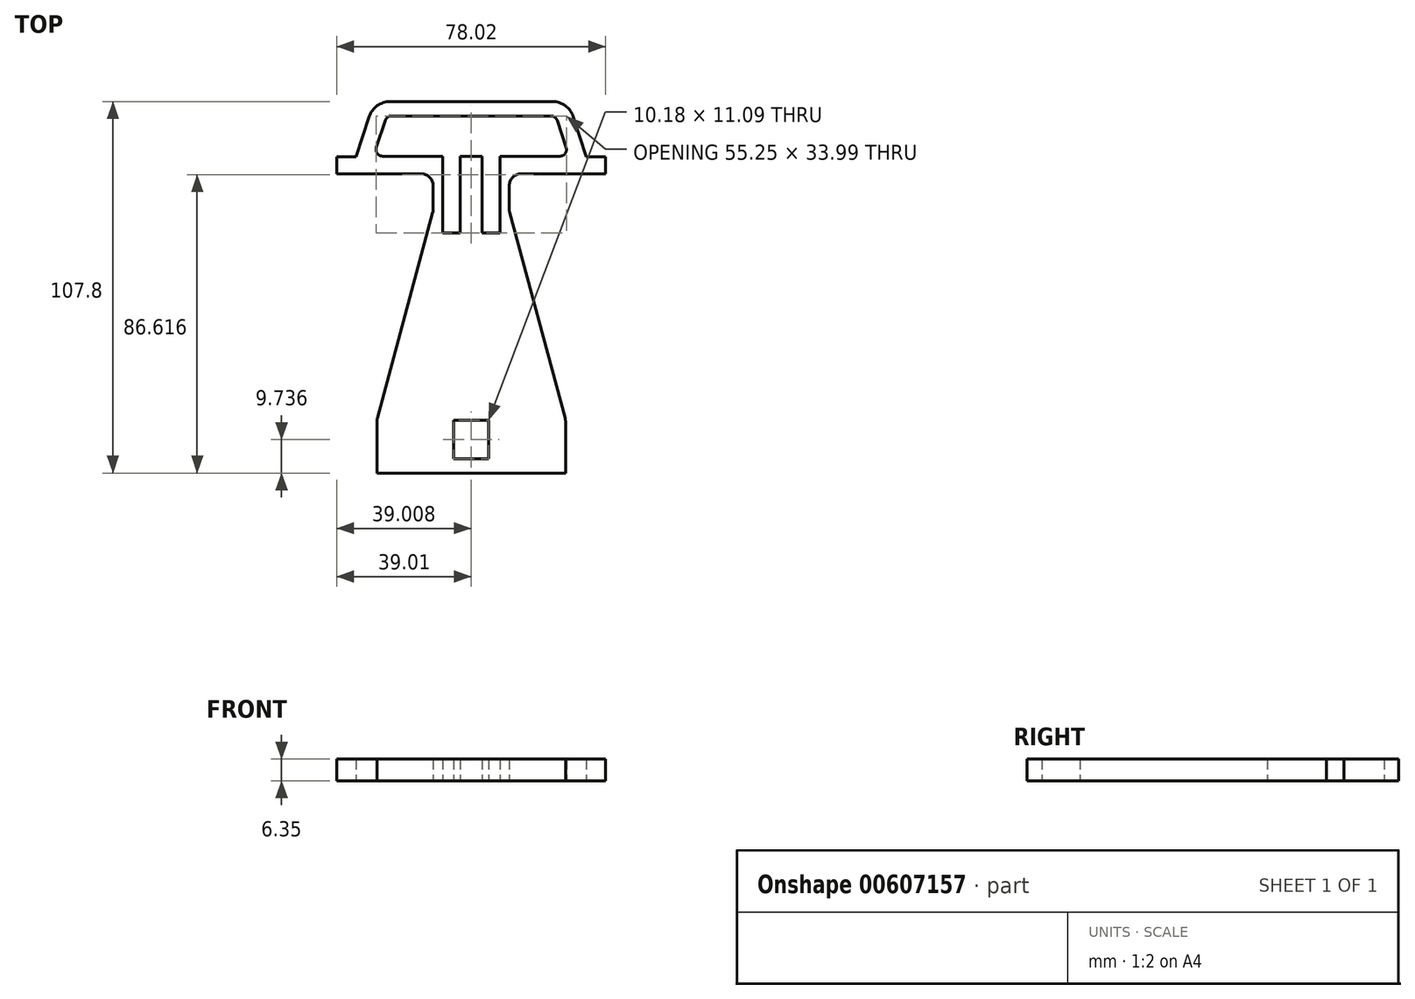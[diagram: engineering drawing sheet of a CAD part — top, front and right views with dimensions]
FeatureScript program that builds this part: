
annotation { "Feature Type Name" : "Feature", "Feature Type Description" : "" }
export const myFeature = defineFeature(function(context is Context, id is Id, definition is map)
    precondition{}
    {
        {
            var Q0;
            Q0=qCreatedBy(makeId("Top.planeOp"),FACE);
            var sketch = newSketch(context, id + "F0", { "sketchPlane" : qUnion([Q0])});
            skLineSegment(sketch, "E0", {"start": v(0, 65.32) * mm, "end": v(0, -59.25) * mm, "construction": true});
            skLineSegment(sketch, "E1", {"start": v(-31.53, 41.22) * mm, "end": v(-25.33, 41.22) * mm});
            skLineSegment(sketch, "E2.MirrorCS", {"start": v(31.53, 41.22) * mm, "end": v(25.33, 41.22) * mm});
            skLineSegment(sketch, "E3", {"start": v(-25.74, 46.3) * mm, "end": v(0, 46.3) * mm});
            skLineSegment(sketch, "E4.MirrorCS", {"start": v(25.72, 46.3) * mm, "end": v(0, 46.3) * mm});
            skPoint(sketch, "E5.visualSharp", {"position": v(-15.2, 41.22) * mm});
            skPoint(sketch, "E6.visualSharp", {"position": v(15.2, 41.22) * mm});
            skLineSegment(sketch, "E7", {"start": v(-33.42, 43.12) * mm, "end": v(-33.42, 46.18) * mm});
            skLineSegment(sketch, "E8", {"start": v(-33.42, 46.18) * mm, "end": v(-29.59, 57.8) * mm});
            skLineSegment(sketch, "E9", {"start": v(-23.56, 62.16) * mm, "end": v(0, 62.16) * mm});
            skLineSegment(sketch, "E10", {"start": v(-27.54, 48.79) * mm, "end": v(-24.93, 56.67) * mm});
            skLineSegment(sketch, "E11", {"start": v(-23.14, 57.97) * mm, "end": v(0, 57.97) * mm});
            skLineSegment(sketch, "E12.MirrorCS", {"start": v(33.42, 43.12) * mm, "end": v(33.42, 46.18) * mm});
            skLineSegment(sketch, "E13.MirrorCS", {"start": v(33.42, 46.18) * mm, "end": v(29.59, 57.8) * mm});
            skLineSegment(sketch, "E14.MirrorCS", {"start": v(23.56, 62.16) * mm, "end": v(0, 62.16) * mm});
            skLineSegment(sketch, "E15.MirrorCS", {"start": v(23.14, 57.97) * mm, "end": v(0, 57.97) * mm});
            skLineSegment(sketch, "E16.MirrorCS", {"start": v(27.53, 48.8) * mm, "end": v(24.93, 56.67) * mm});
            skPoint(sketch, "E17.visualSharp", {"position": v(-28.15, 62.16) * mm});
            skArc(sketch, "E17.filletArc", {"start": v(-23.56, 62.16) * mm, "mid": v(-27.28, 60.95) * mm, "end": v(-29.59, 57.8) * mm});
            skPoint(sketch, "E18.visualSharp", {"position": v(28.15, 62.16) * mm});
            skArc(sketch, "E18.filletArc", {"start": v(29.59, 57.8) * mm, "mid": v(27.28, 60.95) * mm, "end": v(23.56, 62.16) * mm});
            skPoint(sketch, "E19.visualSharp", {"position": v(-33.42, 41.22) * mm});
            skArc(sketch, "E19.filletArc", {"start": v(-33.42, 43.12) * mm, "mid": v(-32.87, 41.78) * mm, "end": v(-31.53, 41.22) * mm});
            skPoint(sketch, "E20.visualSharp", {"position": v(33.42, 41.22) * mm});
            skArc(sketch, "E20.filletArc", {"start": v(31.53, 41.22) * mm, "mid": v(32.87, 41.78) * mm, "end": v(33.42, 43.12) * mm});
            skPoint(sketch, "E21.visualSharp", {"position": v(-28.36, 46.3) * mm});
            skArc(sketch, "E21.filletArc", {"start": v(-27.54, 48.79) * mm, "mid": v(-27.27, 47.09) * mm, "end": v(-25.74, 46.3) * mm});
            skPoint(sketch, "E22.visualSharp", {"position": v(-24.5, 57.97) * mm});
            skArc(sketch, "E22.filletArc", {"start": v(-23.14, 57.97) * mm, "mid": v(-24.24, 57.6) * mm, "end": v(-24.93, 56.67) * mm});
            skPoint(sketch, "E23.visualSharp", {"position": v(24.5, 57.97) * mm});
            skArc(sketch, "E23.filletArc", {"start": v(24.93, 56.67) * mm, "mid": v(24.24, 57.6) * mm, "end": v(23.14, 57.97) * mm});
            skPoint(sketch, "E24.visualSharp", {"position": v(28.36, 46.3) * mm});
            skArc(sketch, "E24.filletArc", {"start": v(25.72, 46.3) * mm, "mid": v(27.27, 47.1) * mm, "end": v(27.53, 48.8) * mm});
            skLineSegment(sketch, "E25", {"start": v(-25.33, 41.22) * mm, "end": v(-14.55, 41.22) * mm});
            skLineSegment(sketch, "E26", {"start": v(-11.03, 37.7) * mm, "end": v(-11.03, 30.91) * mm});
            skLineSegment(sketch, "E27", {"start": v(-11.15, 30) * mm, "end": v(-27.22, -29.67) * mm});
            skLineSegment(sketch, "E28", {"start": v(-31.53, -45.64) * mm, "end": v(0, -45.64) * mm});
            skLineSegment(sketch, "E29.MirrorCS", {"start": v(11.03, 37.7) * mm, "end": v(11.03, 30.91) * mm});
            skLineSegment(sketch, "E30.MirrorCS", {"start": v(25.33, 41.22) * mm, "end": v(14.55, 41.22) * mm});
            skLineSegment(sketch, "E31.MirrorCS", {"start": v(11.15, 30) * mm, "end": v(27.22, -29.67) * mm});
            skLineSegment(sketch, "E32.MirrorCS", {"start": v(31.53, -45.64) * mm, "end": v(0, -45.64) * mm});
            skPoint(sketch, "E33.visualSharp", {"position": v(-11.03, 41.22) * mm});
            skArc(sketch, "E33.filletArc", {"start": v(-11.03, 37.7) * mm, "mid": v(-12.06, 40.19) * mm, "end": v(-14.55, 41.22) * mm});
            skPoint(sketch, "E34.visualSharp", {"position": v(11.03, 41.22) * mm});
            skArc(sketch, "E34.filletArc", {"start": v(14.55, 41.22) * mm, "mid": v(12.06, 40.19) * mm, "end": v(11.03, 37.7) * mm});
            skPoint(sketch, "E35.visualSharp", {"position": v(11.03, 30.45) * mm});
            skArc(sketch, "E35.filletArc", {"start": v(11.03, 30.91) * mm, "mid": v(11.06, 30.45) * mm, "end": v(11.15, 30) * mm});
            skPoint(sketch, "E36.visualSharp", {"position": v(-11.03, 30.45) * mm});
            skArc(sketch, "E36.filletArc", {"start": v(-11.15, 30) * mm, "mid": v(-11.06, 30.45) * mm, "end": v(-11.03, 30.91) * mm});
            skLineSegment(sketch, "E37", {"start": v(-27.35, -30.58) * mm, "end": v(-27.35, -68.57) * mm});
            skLineSegment(sketch, "E38.MirrorCS", {"start": v(27.35, -30.58) * mm, "end": v(27.35, -68.57) * mm});
            skPoint(sketch, "E39.newPointA", {"position": v(-31.53, -45.64) * mm});
            skPoint(sketch, "E39.newPointB", {"position": v(-27.35, 4.35) * mm});
            skArc(sketch, "E39.filletArc", {"start": v(-27.22, -29.67) * mm, "mid": v(-27.31, -30.12) * mm, "end": v(-27.35, -30.58) * mm});
            skPoint(sketch, "E40.newPointA", {"position": v(31.53, -45.64) * mm});
            skPoint(sketch, "E40.newPointB", {"position": v(27.35, 4.35) * mm});
            skArc(sketch, "E40.filletArc", {"start": v(27.35, -30.58) * mm, "mid": v(27.31, -30.12) * mm, "end": v(27.22, -29.67) * mm});
            skLineSegment(sketch, "E41.bottom", {"start": v(-8.3, 49.38) * mm, "end": v(-3.16, 49.38) * mm});
            skLineSegment(sketch, "E41.top", {"start": v(-8.3, 23.98) * mm, "end": v(-3.16, 23.98) * mm});
            skLineSegment(sketch, "E41.left", {"start": v(-8.3, 49.38) * mm, "end": v(-8.3, 23.98) * mm});
            skLineSegment(sketch, "E41.right", {"start": v(-3.16, 49.38) * mm, "end": v(-3.16, 23.98) * mm});
            skLineSegment(sketch, "E42.bottom", {"start": v(0, -30.36) * mm, "end": v(-5.09, -30.36) * mm});
            skLineSegment(sketch, "E42.top", {"start": v(0, -41.45) * mm, "end": v(-5.09, -41.45) * mm});
            skLineSegment(sketch, "E42.left", {"start": v(0, -30.36) * mm, "end": v(0, -41.45) * mm});
            skLineSegment(sketch, "E42.right", {"start": v(-5.09, -30.36) * mm, "end": v(-5.09, -41.45) * mm});
            skLineSegment(sketch, "E43.MirrorCS", {"start": v(3.16, 49.38) * mm, "end": v(3.16, 23.98) * mm});
            skLineSegment(sketch, "E44.MirrorCS", {"start": v(8.3, 23.98) * mm, "end": v(3.16, 23.98) * mm});
            skLineSegment(sketch, "E45.MirrorCS", {"start": v(8.3, 49.38) * mm, "end": v(8.3, 23.98) * mm});
            skLineSegment(sketch, "E46.MirrorCS", {"start": v(8.3, 49.38) * mm, "end": v(3.16, 49.38) * mm});
            skLineSegment(sketch, "E47.MirrorCS", {"start": v(0, -41.45) * mm, "end": v(5.09, -41.45) * mm});
            skLineSegment(sketch, "E48.MirrorCS", {"start": v(5.09, -30.36) * mm, "end": v(5.09, -41.45) * mm});
            skLineSegment(sketch, "E49.MirrorCS", {"start": v(0, -30.36) * mm, "end": v(5.09, -30.36) * mm});
            skLineSegment(sketch, "E50", {"start": v(-33.42, 46.18) * mm, "end": v(-39.01, 46.18) * mm});
            skLineSegment(sketch, "E51", {"start": v(-39.01, 46.18) * mm, "end": v(-39.01, 41.22) * mm});
            skLineSegment(sketch, "E52", {"start": v(-39.01, 41.22) * mm, "end": v(-31.53, 41.22) * mm});
            skLineSegment(sketch, "E53.MirrorCS", {"start": v(39.01, 41.22) * mm, "end": v(31.53, 41.22) * mm});
            skLineSegment(sketch, "E54.MirrorCS", {"start": v(33.42, 46.18) * mm, "end": v(39.01, 46.18) * mm});
            skLineSegment(sketch, "E55.MirrorCS", {"start": v(39.01, 46.18) * mm, "end": v(39.01, 41.22) * mm});
            skArc(sketch, "E56.MirrorCS", {"start": v(33.42, 43.12) * mm, "mid": v(32.87, 41.78) * mm, "end": v(31.53, 41.22) * mm});
            skSolve(sketch);
        }
        {
            var Q0;
            Q0 = qSketchRegion(id + "F0", true);
            extrude(context, id + "F1", {"entities" : qUnion([Q0]), "depth" : 6.35 * mm, "offsetDistance" : 25.4 * mm});
        }
    });
